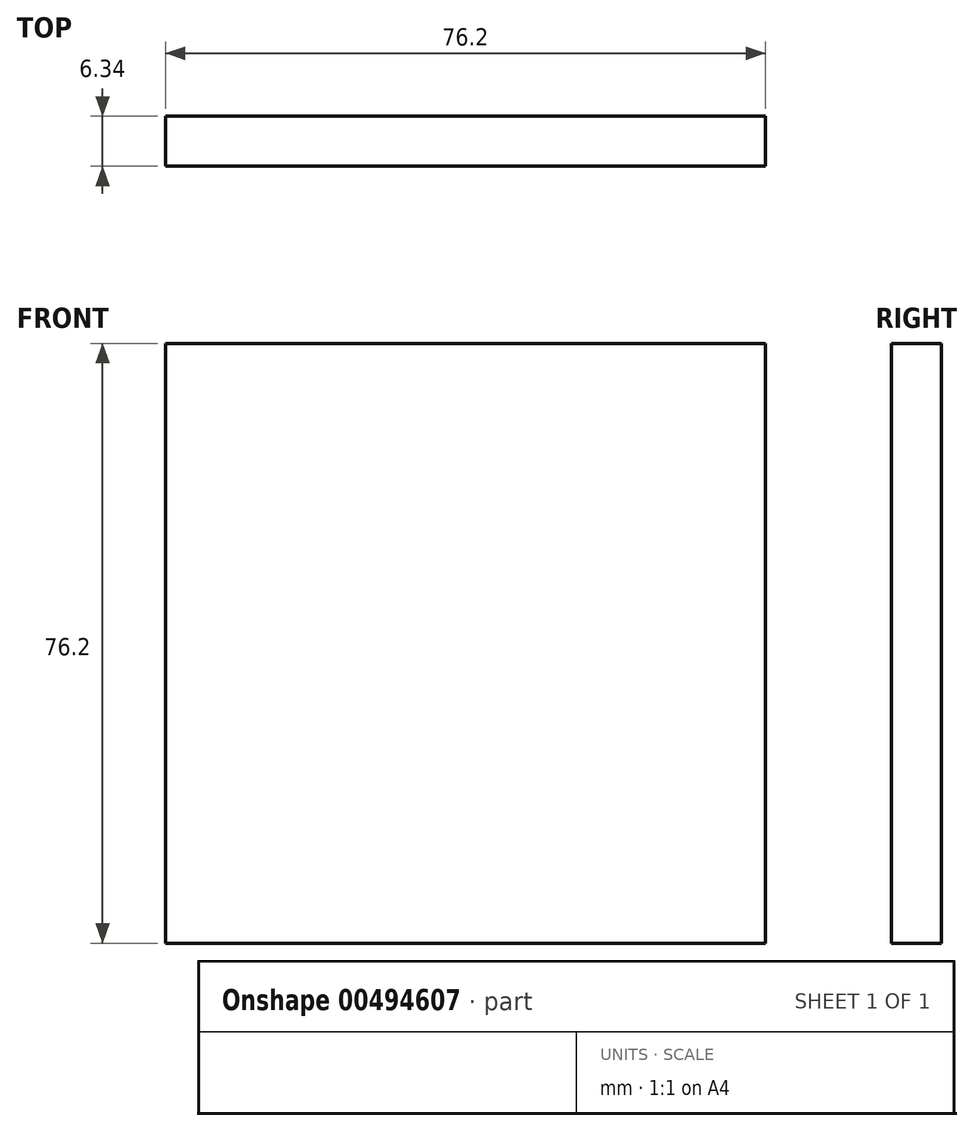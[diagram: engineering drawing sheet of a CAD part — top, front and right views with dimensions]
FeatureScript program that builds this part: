
annotation { "Feature Type Name" : "Feature", "Feature Type Description" : "" }
export const myFeature = defineFeature(function(context is Context, id is Id, definition is map)
    precondition{}
    {
        {
            var Q0;
            Q0=qCreatedBy(makeId("Top.planeOp"),FACE);
            var sketch = newSketch(context, id + "F0", { "sketchPlane" : qUnion([Q0])});
            skLineSegment(sketch, "E0", {"start": v(-76.2, -3.18) * mm, "end": v(0, -3.18) * mm});
            skLineSegment(sketch, "E1", {"start": v(-76.2, -3.18) * mm, "end": v(-76.2, 3.18) * mm});
            skLineSegment(sketch, "E2", {"start": v(-76.2, 3.18) * mm, "end": v(0, 3.18) * mm});
            skLineSegment(sketch, "E3", {"start": v(0, 3.18) * mm, "end": v(0, -3.18) * mm});
            skPoint(sketch, "E4", {"position": v(0, 0) * mm});
            skSolve(sketch);
        }
        {
            var Q0;
            Q0 = qSketchRegion(id + "F0", true);
            extrude(context, id + "F1", {"entities" : qUnion([Q0]), "depth" : 76.2 * mm});
        }
    });
